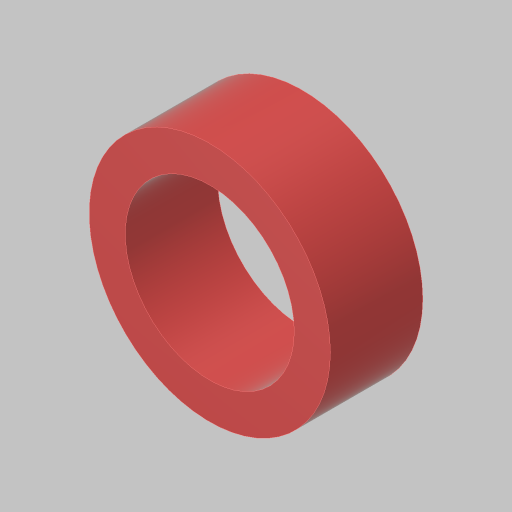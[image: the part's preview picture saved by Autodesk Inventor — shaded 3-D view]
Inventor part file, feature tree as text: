
AUTODESK INVENTOR PART (.ipt)
format: ipt  version: 2023.5 (Build 275446000, 446)  size: 113,152 bytes
history: native  units: in
note: dims shown in document units (in); Inventor stores cm internally (conversion verified against a paired STEP export)
features: extrude x1, sketch x1
ambient origin geometry x8: Origin, YZ Plane, XZ Plane, XY Plane, X Axis, Y Axis, Z Axis, Center Point
bodies: Solid1 (feature_tree)
feature tree (2):
  extrude  "Extrusion1"  Depth=0.32in
  sketch  "Sketch1"  dims[d0=0.585in d1=0.125in d2=0.32in d3=0.0in]
